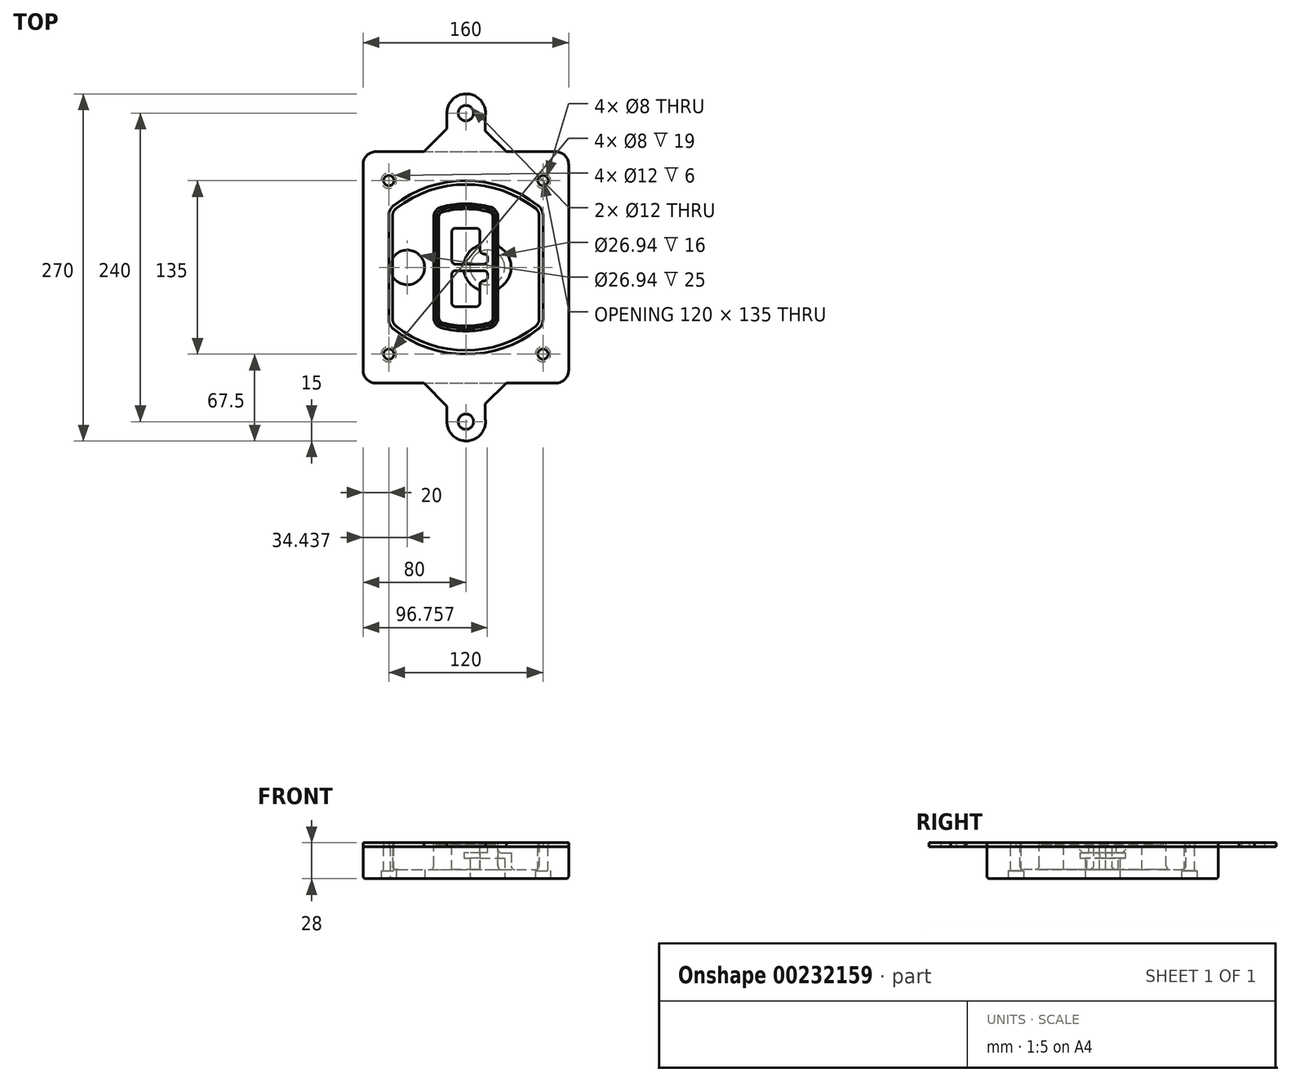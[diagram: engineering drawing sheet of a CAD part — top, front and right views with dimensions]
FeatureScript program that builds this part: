
annotation { "Feature Type Name" : "Feature", "Feature Type Description" : "" }
export const myFeature = defineFeature(function(context is Context, id is Id, definition is map)
    precondition{}
    {
        {
            var Q0;
            Q0=qCreatedBy(makeId("Top.planeOp"),FACE);
            var sketch = newSketch(context, id + "F0", { "sketchPlane" : qUnion([Q0])});
            skPoint(sketch, "E0.rect.middle", {"position": v(0, 0) * mm});
            skLineSegment(sketch, "E1.bottom", {"start": v(-70, -90) * mm, "end": v(70, -90) * mm});
            skLineSegment(sketch, "E1.top", {"start": v(-70, 90) * mm, "end": v(70, 90) * mm});
            skLineSegment(sketch, "E1.left", {"start": v(-80, -80) * mm, "end": v(-80, 80) * mm});
            skLineSegment(sketch, "E1.right", {"start": v(80, -80) * mm, "end": v(80, 80) * mm});
            skLineSegment(sketch, "E2", {"start": v(-80, 90) * mm, "end": v(80, -90) * mm, "construction": true});
            skLineSegment(sketch, "E3", {"start": v(80, 90) * mm, "end": v(-80, -90) * mm, "construction": true});
            skCircle(sketch, "E4", {"center": v(-60, 67.5) * mm, "radius": 4 * mm});
            skCircle(sketch, "E5", {"center": v(60, 67.5) * mm, "radius": 4 * mm});
            skCircle(sketch, "E6", {"center": v(60, -67.5) * mm, "radius": 4 * mm});
            skCircle(sketch, "E7", {"center": v(-60, -67.5) * mm, "radius": 4 * mm});
            skLineSegment(sketch, "E8", {"start": v(-60, 67.5) * mm, "end": v(60, 67.5) * mm, "construction": true});
            skLineSegment(sketch, "E9", {"start": v(60, 67.5) * mm, "end": v(60, -67.5) * mm, "construction": true});
            skLineSegment(sketch, "E10", {"start": v(60, -67.5) * mm, "end": v(-60, -67.5) * mm, "construction": true});
            skLineSegment(sketch, "E11", {"start": v(-60, -67.5) * mm, "end": v(-60, 67.5) * mm, "construction": true});
            skLineSegment(sketch, "E12", {"start": v(-60, 40.3) * mm, "end": v(-60, -40.3) * mm});
            skLineSegment(sketch, "E13", {"start": v(60, 40.3) * mm, "end": v(60, -40.3) * mm});
            skArc(sketch, "E14", {"start": v(56.15, 48.18) * mm, "mid": v(0, 67.5) * mm, "end": v(-56.15, 48.18) * mm});
            skArc(sketch, "E15", {"start": v(-56.15, -48.18) * mm, "mid": v(0, -67.5) * mm, "end": v(56.15, -48.18) * mm});
            skLineSegment(sketch, "E16", {"start": v(-60, 0) * mm, "end": v(60, 0) * mm, "construction": true});
            skPoint(sketch, "E17.visualSharp", {"position": v(-60, -45) * mm});
            skArc(sketch, "E17.filletArc", {"start": v(-60, -40.3) * mm, "mid": v(-58.99, -44.68) * mm, "end": v(-56.15, -48.18) * mm});
            skPoint(sketch, "E18.visualSharp", {"position": v(-60, 45) * mm});
            skArc(sketch, "E18.filletArc", {"start": v(-56.15, 48.18) * mm, "mid": v(-58.99, 44.68) * mm, "end": v(-60, 40.3) * mm});
            skPoint(sketch, "E19.visualSharp", {"position": v(60, 45) * mm});
            skArc(sketch, "E19.filletArc", {"start": v(60, 40.3) * mm, "mid": v(58.99, 44.68) * mm, "end": v(56.15, 48.18) * mm});
            skPoint(sketch, "E20.visualSharp", {"position": v(60, -45) * mm});
            skArc(sketch, "E20.filletArc", {"start": v(56.15, -48.18) * mm, "mid": v(58.99, -44.68) * mm, "end": v(60, -40.3) * mm});
            skPoint(sketch, "E21.visualSharp", {"position": v(-80, 90) * mm});
            skArc(sketch, "E21.filletArc", {"start": v(-70, 90) * mm, "mid": v(-77.07, 87.07) * mm, "end": v(-80, 80) * mm});
            skPoint(sketch, "E22.visualSharp", {"position": v(80, 90) * mm});
            skArc(sketch, "E22.filletArc", {"start": v(80, 80) * mm, "mid": v(77.07, 87.07) * mm, "end": v(70, 90) * mm});
            skPoint(sketch, "E23.visualSharp", {"position": v(80, -90) * mm});
            skArc(sketch, "E23.filletArc", {"start": v(70, -90) * mm, "mid": v(77.07, -87.07) * mm, "end": v(80, -80) * mm});
            skPoint(sketch, "E24.visualSharp", {"position": v(-80, -90) * mm});
            skArc(sketch, "E24.filletArc", {"start": v(-80, -80) * mm, "mid": v(-77.07, -87.07) * mm, "end": v(-70, -90) * mm});
            skArc(sketch, "E25.0", {"start": v(57, 40.3) * mm, "mid": v(56.3, 43.36) * mm, "end": v(54.3, 45.81) * mm});
            skLineSegment(sketch, "E25.1", {"start": v(57, 40.3) * mm, "end": v(57, -40.3) * mm});
            skArc(sketch, "E25.2", {"start": v(54.3, -45.81) * mm, "mid": v(56.3, -43.36) * mm, "end": v(57, -40.3) * mm});
            skArc(sketch, "E25.3", {"start": v(-54.3, -45.81) * mm, "mid": v(0, -64.5) * mm, "end": v(54.3, -45.81) * mm});
            skArc(sketch, "E25.4", {"start": v(-57, -40.3) * mm, "mid": v(-56.3, -43.36) * mm, "end": v(-54.3, -45.81) * mm});
            skArc(sketch, "E25.5", {"start": v(54.3, 45.81) * mm, "mid": v(0, 64.5) * mm, "end": v(-54.3, 45.81) * mm});
            skLineSegment(sketch, "E25.6", {"start": v(-57, 40.3) * mm, "end": v(-57, -40.3) * mm});
            skArc(sketch, "E25.7", {"start": v(-54.3, 45.81) * mm, "mid": v(-56.3, 43.36) * mm, "end": v(-57, 40.3) * mm});
            skArc(sketch, "E26.0", {"start": v(-58.62, 51.33) * mm, "mid": v(-62.58, 46.43) * mm, "end": v(-64, 40.3) * mm});
            skArc(sketch, "E26.1", {"start": v(58.62, 51.33) * mm, "mid": v(0, 71.5) * mm, "end": v(-58.62, 51.33) * mm});
            skArc(sketch, "E26.2", {"start": v(64, 40.3) * mm, "mid": v(62.58, 46.43) * mm, "end": v(58.62, 51.33) * mm});
            skLineSegment(sketch, "E26.3", {"start": v(64, 40.3) * mm, "end": v(64, -40.3) * mm});
            skArc(sketch, "E26.4", {"start": v(58.62, -51.33) * mm, "mid": v(62.58, -46.43) * mm, "end": v(64, -40.3) * mm});
            skLineSegment(sketch, "E26.5", {"start": v(-64, 40.3) * mm, "end": v(-64, -40.3) * mm});
            skArc(sketch, "E26.6", {"start": v(-58.62, -51.33) * mm, "mid": v(0, -71.5) * mm, "end": v(58.62, -51.33) * mm});
            skArc(sketch, "E26.7", {"start": v(-64, -40.3) * mm, "mid": v(-62.58, -46.43) * mm, "end": v(-58.62, -51.33) * mm});
            skSolve(sketch);
        }
        {
            var Q0;
            Q0=makeQuery(id+"F0.imprint","IMPRINT",FACE,{"disambiguationData":[TD([[makeQuery(id+"F0.imprint","IMPRINT",EDGE,{"derivedFrom":sQuery(id+"F0.wireOp",EDGE,"E1.bottom")}),1.0]])]});
            var Q1;
            Q1=makeQuery(id+"F0.imprint","IMPRINT",FACE,{"disambiguationData":[TD([[makeQuery(id+"F0.imprint","IMPRINT",EDGE,{"derivedFrom":sQuery(id+"F0.wireOp",EDGE,"E12")}),1.0]])]});
            var Q2;
            Q2=makeQuery(id+"F0.imprint","IMPRINT",FACE,{"disambiguationData":[TD([[makeQuery(id+"F0.imprint","IMPRINT",EDGE,{"derivedFrom":sQuery(id+"F0.wireOp",EDGE,"E25.0")}),1.0]])]});
            var Q3;
            Q3=makeQuery(id+"F0.imprint","IMPRINT",FACE,{"disambiguationData":[TD([[makeQuery(id+"F0.imprint","IMPRINT",EDGE,{"derivedFrom":sQuery(id+"F0.wireOp",EDGE,"E12")}),-1.0]])]});
            extrude(context, id + "F1", {"entities" : qUnion([Q0, Q1, Q2, Q3]), "oppositeDirection" : true, "depth" : 25 * mm});
        }
        {
            var Q0;
            Q0=makeQuery(id+"F0.imprint","IMPRINT",FACE,{"disambiguationData":[TD([[makeQuery(id+"F0.imprint","IMPRINT",EDGE,{"derivedFrom":sQuery(id+"F0.wireOp",EDGE,"E12")}),1.0]])]});
            extrude(context, id + "F2", {"entities" : qUnion([Q0]), "operationType" : NewBodyOperationType.ADD, "depth" : 3 * mm});
        }
        {
            var Q0;
            Q0=makeQuery(id+"F0.imprint","IMPRINT",FACE,{"disambiguationData":[TD([[makeQuery(id+"F0.imprint","IMPRINT",EDGE,{"derivedFrom":sQuery(id+"F0.wireOp",EDGE,"E25.0")}),1.0]])]});
            extrude(context, id + "F3", {"entities" : qUnion([Q0]), "operationType" : NewBodyOperationType.REMOVE, "oppositeDirection" : true, "depth" : 18 * mm});
        }
        {
            var Q0;
            Q0=makeQuery(id+"F2.opExtrude","CAP_FACE",FACE,{"disambiguationData":[OSD([sQuery(id+"F0.wireOp",EDGE,"E12"),sQuery(id+"F0.wireOp",EDGE,"E13"),sQuery(id+"F0.wireOp",EDGE,"E14"),sQuery(id+"F0.wireOp",EDGE,"E15"),sQuery(id+"F0.wireOp",EDGE,"E17.filletArc"),sQuery(id+"F0.wireOp",EDGE,"E18.filletArc"),sQuery(id+"F0.wireOp",EDGE,"E19.filletArc"),sQuery(id+"F0.wireOp",EDGE,"E20.filletArc"),sQuery(id+"F0.wireOp",EDGE,"E25.0"),sQuery(id+"F0.wireOp",EDGE,"E25.1"),sQuery(id+"F0.wireOp",EDGE,"E25.2"),sQuery(id+"F0.wireOp",EDGE,"E25.3"),sQuery(id+"F0.wireOp",EDGE,"E25.4"),sQuery(id+"F0.wireOp",EDGE,"E25.5"),sQuery(id+"F0.wireOp",EDGE,"E25.6"),sQuery(id+"F0.wireOp",EDGE,"E25.7")])],"isStart":false});
            var sketch = newSketch(context, id + "F4", { "sketchPlane" : qUnion([Q0])});
            skArc(sketch, "E27.0", {"start": v(-19.08, -46.97) * mm, "mid": v(0, -49.5) * mm, "end": v(19.08, -46.97) * mm});
            skArc(sketch, "E28.0", {"start": v(19.08, 46.97) * mm, "mid": v(0, 49.5) * mm, "end": v(-19.08, 46.97) * mm});
            skLineSegment(sketch, "E29", {"start": v(-25, 39.25) * mm, "end": v(-25, -39.25) * mm});
            skLineSegment(sketch, "E30", {"start": v(25, 39.25) * mm, "end": v(25, -39.25) * mm});
            skLineSegment(sketch, "E31", {"start": v(-25, 45.1) * mm, "end": v(25, 45.1) * mm, "construction": true});
            skLineSegment(sketch, "E32", {"start": v(-25, -45.1) * mm, "end": v(25, -45.1) * mm, "construction": true});
            skPoint(sketch, "E33.visualSharp", {"position": v(-25, 45.1) * mm});
            skArc(sketch, "E33.filletArc", {"start": v(-19.08, 46.97) * mm, "mid": v(-23.35, 44.11) * mm, "end": v(-25, 39.25) * mm});
            skPoint(sketch, "E34.visualSharp", {"position": v(25, 45.1) * mm});
            skArc(sketch, "E34.filletArc", {"start": v(25, 39.25) * mm, "mid": v(23.35, 44.11) * mm, "end": v(19.08, 46.97) * mm});
            skPoint(sketch, "E35.visualSharp", {"position": v(25, -45.1) * mm});
            skArc(sketch, "E35.filletArc", {"start": v(19.08, -46.97) * mm, "mid": v(23.35, -44.11) * mm, "end": v(25, -39.25) * mm});
            skPoint(sketch, "E36.visualSharp", {"position": v(-25, -45.1) * mm});
            skArc(sketch, "E36.filletArc", {"start": v(-25, -39.25) * mm, "mid": v(-23.35, -44.11) * mm, "end": v(-19.08, -46.97) * mm});
            skArc(sketch, "E37.0", {"start": v(54.3, 45.81) * mm, "mid": v(0, 64.5) * mm, "end": v(-54.3, 45.81) * mm});
            skArc(sketch, "E37.1", {"start": v(-54.3, 45.81) * mm, "mid": v(-56.3, 43.36) * mm, "end": v(-57, 40.3) * mm});
            skLineSegment(sketch, "E37.2", {"start": v(-57, 40.3) * mm, "end": v(-57, -40.3) * mm});
            skArc(sketch, "E37.3", {"start": v(-57, -40.3) * mm, "mid": v(-56.3, -43.36) * mm, "end": v(-54.3, -45.81) * mm});
            skArc(sketch, "E37.4", {"start": v(-54.3, -45.81) * mm, "mid": v(0, -64.5) * mm, "end": v(54.3, -45.81) * mm});
            skArc(sketch, "E37.5", {"start": v(54.3, -45.81) * mm, "mid": v(56.3, -43.36) * mm, "end": v(57, -40.3) * mm});
            skLineSegment(sketch, "E37.6", {"start": v(57, 40.3) * mm, "end": v(57, -40.3) * mm});
            skArc(sketch, "E37.7", {"start": v(57, 40.3) * mm, "mid": v(56.3, 43.36) * mm, "end": v(54.3, 45.81) * mm});
            skLineSegment(sketch, "E38.0", {"start": v(23, 39.25) * mm, "end": v(23, -39.25) * mm});
            skArc(sketch, "E38.1", {"start": v(18.56, -45.04) * mm, "mid": v(21.76, -42.9) * mm, "end": v(23, -39.25) * mm});
            skArc(sketch, "E38.2", {"start": v(-18.56, -45.04) * mm, "mid": v(0, -47.5) * mm, "end": v(18.56, -45.04) * mm});
            skArc(sketch, "E38.3", {"start": v(-23, -39.25) * mm, "mid": v(-21.76, -42.9) * mm, "end": v(-18.56, -45.04) * mm});
            skLineSegment(sketch, "E38.4", {"start": v(-23, 39.25) * mm, "end": v(-23, -39.25) * mm});
            skArc(sketch, "E38.5", {"start": v(23, 39.25) * mm, "mid": v(21.76, 42.9) * mm, "end": v(18.56, 45.04) * mm});
            skArc(sketch, "E38.6", {"start": v(-18.56, 45.04) * mm, "mid": v(-21.76, 42.9) * mm, "end": v(-23, 39.25) * mm});
            skArc(sketch, "E38.7", {"start": v(18.56, 45.04) * mm, "mid": v(0, 47.5) * mm, "end": v(-18.56, 45.04) * mm});
            skArc(sketch, "E39.0", {"start": v(21, 39.25) * mm, "mid": v(20.18, 41.68) * mm, "end": v(18.04, 43.1) * mm});
            skLineSegment(sketch, "E39.1", {"start": v(21, 39.25) * mm, "end": v(21, -39.25) * mm});
            skArc(sketch, "E39.2", {"start": v(18.04, -43.1) * mm, "mid": v(20.18, -41.68) * mm, "end": v(21, -39.25) * mm});
            skArc(sketch, "E39.3", {"start": v(-18.04, -43.1) * mm, "mid": v(0, -45.5) * mm, "end": v(18.04, -43.1) * mm});
            skArc(sketch, "E39.4", {"start": v(-21, -39.25) * mm, "mid": v(-20.18, -41.68) * mm, "end": v(-18.04, -43.1) * mm});
            skArc(sketch, "E39.5", {"start": v(18.04, 43.1) * mm, "mid": v(0, 45.5) * mm, "end": v(-18.04, 43.1) * mm});
            skLineSegment(sketch, "E39.6", {"start": v(-21, 39.25) * mm, "end": v(-21, -39.25) * mm});
            skArc(sketch, "E39.7", {"start": v(-18.04, 43.1) * mm, "mid": v(-20.18, 41.68) * mm, "end": v(-21, 39.25) * mm});
            skLineSegment(sketch, "E40", {"start": v(-25, 0) * mm, "end": v(25, 0) * mm, "construction": true});
            skLineSegment(sketch, "E41", {"start": v(-11, 5.5) * mm, "end": v(-11, 27.5) * mm});
            skLineSegment(sketch, "E42", {"start": v(-8, 30.5) * mm, "end": v(8, 30.5) * mm});
            skLineSegment(sketch, "E43", {"start": v(11, 27.5) * mm, "end": v(11, 13.5) * mm});
            skLineSegment(sketch, "E44", {"start": v(14, 10.5) * mm, "end": v(14, 10.5) * mm});
            skLineSegment(sketch, "E45", {"start": v(17, 7.5) * mm, "end": v(17, 5.5) * mm});
            skLineSegment(sketch, "E46", {"start": v(14, 2.5) * mm, "end": v(-8, 2.5) * mm});
            skPoint(sketch, "E47.visualSharp", {"position": v(-11, 30.5) * mm});
            skArc(sketch, "E47.filletArc", {"start": v(-8, 30.5) * mm, "mid": v(-10.12, 29.62) * mm, "end": v(-11, 27.5) * mm});
            skPoint(sketch, "E48.visualSharp", {"position": v(11, 30.5) * mm});
            skArc(sketch, "E48.filletArc", {"start": v(11, 27.5) * mm, "mid": v(10.12, 29.62) * mm, "end": v(8, 30.5) * mm});
            skPoint(sketch, "E49.visualSharp", {"position": v(11, 10.5) * mm});
            skArc(sketch, "E49.filletArc", {"start": v(11, 13.5) * mm, "mid": v(11.88, 11.38) * mm, "end": v(14, 10.5) * mm});
            skPoint(sketch, "E50.visualSharp", {"position": v(17, 10.5) * mm});
            skArc(sketch, "E50.filletArc", {"start": v(17, 7.5) * mm, "mid": v(16.12, 9.62) * mm, "end": v(14, 10.5) * mm});
            skPoint(sketch, "E51.visualSharp", {"position": v(17, 2.5) * mm});
            skArc(sketch, "E51.filletArc", {"start": v(14, 2.5) * mm, "mid": v(16.12, 3.38) * mm, "end": v(17, 5.5) * mm});
            skPoint(sketch, "E52.visualSharp", {"position": v(-11, 2.5) * mm});
            skArc(sketch, "E52.filletArc", {"start": v(-11, 5.5) * mm, "mid": v(-10.12, 3.38) * mm, "end": v(-8, 2.5) * mm});
            skLineSegment(sketch, "E53.0.MirrorCS", {"start": v(14, -2.5) * mm, "end": v(-8, -2.5) * mm});
            skArc(sketch, "E54.0.MirrorCS", {"start": v(-11, -5.5) * mm, "mid": v(-10.12, -3.38) * mm, "end": v(-8, -2.5) * mm});
            skLineSegment(sketch, "E55.0.MirrorCS", {"start": v(-11, -5.5) * mm, "end": v(-11, -27.5) * mm});
            skArc(sketch, "E56.0.MirrorCS", {"start": v(-8, -30.5) * mm, "mid": v(-10.12, -29.62) * mm, "end": v(-11, -27.5) * mm});
            skLineSegment(sketch, "E57.0.MirrorCS", {"start": v(-8, -30.5) * mm, "end": v(8, -30.5) * mm});
            skArc(sketch, "E58.0.MirrorCS", {"start": v(11, -27.5) * mm, "mid": v(10.12, -29.62) * mm, "end": v(8, -30.5) * mm});
            skLineSegment(sketch, "E59.0.MirrorCS", {"start": v(11, -27.5) * mm, "end": v(11, -13.5) * mm});
            skArc(sketch, "E60.0.MirrorCS", {"start": v(11, -13.5) * mm, "mid": v(11.88, -11.38) * mm, "end": v(14, -10.5) * mm});
            skArc(sketch, "E61.0.MirrorCS", {"start": v(17, -7.5) * mm, "mid": v(16.12, -9.62) * mm, "end": v(14, -10.5) * mm});
            skLineSegment(sketch, "E62.0.MirrorCS", {"start": v(17, -7.5) * mm, "end": v(17, -5.5) * mm});
            skArc(sketch, "E63.0.MirrorCS", {"start": v(14, -2.5) * mm, "mid": v(16.12, -3.38) * mm, "end": v(17, -5.5) * mm});
            skSolve(sketch);
        }
        {
            var Q0;
            Q0=makeQuery(id+"F4.imprint","IMPRINT",FACE,{"disambiguationData":[TD([[makeQuery(id+"F4.imprint","IMPRINT",EDGE,{"derivedFrom":sQuery(id+"F4.wireOp",EDGE,"E27.0")}),1.0]])]});
            var Q1;
            Q1=makeQuery(id+"F4.imprint","IMPRINT",FACE,{"disambiguationData":[TD([[makeQuery(id+"F4.imprint","IMPRINT",EDGE,{"derivedFrom":sQuery(id+"F4.wireOp",EDGE,"E38.0")}),-1.0]])]});
            var Q2;
            Q2=makeQuery(id+"F4.imprint","IMPRINT",FACE,{"disambiguationData":[TD([[makeQuery(id+"F4.imprint","IMPRINT",EDGE,{"derivedFrom":sQuery(id+"F4.wireOp",EDGE,"E39.0")}),1.0]])]});
            extrude(context, id + "F5", {"entities" : qUnion([Q0, Q1, Q2]), "operationType" : NewBodyOperationType.ADD, "endBound" : BoundingType.UP_TO_NEXT, "oppositeDirection" : true, "depth" : 25 * mm});
        }
        {
            var Q0;
            Q0=makeQuery(id+"F4.imprint","IMPRINT",FACE,{"disambiguationData":[TD([[makeQuery(id+"F4.imprint","IMPRINT",EDGE,{"derivedFrom":sQuery(id+"F4.wireOp",EDGE,"E38.0")}),-1.0]])]});
            extrude(context, id + "F6", {"entities" : qUnion([Q0]), "operationType" : NewBodyOperationType.REMOVE, "oppositeDirection" : true, "depth" : 2 * mm});
        }
        {
            var Q0;
            Q0=makeQuery(id+"F1.opExtrude","CAP_FACE",FACE,{"disambiguationData":[OSD([sQuery(id+"F0.wireOp",EDGE,"E1.bottom"),sQuery(id+"F0.wireOp",EDGE,"E1.top"),sQuery(id+"F0.wireOp",EDGE,"E1.left"),sQuery(id+"F0.wireOp",EDGE,"E1.right"),sQuery(id+"F0.wireOp",EDGE,"E4"),sQuery(id+"F0.wireOp",EDGE,"E5"),sQuery(id+"F0.wireOp",EDGE,"E6"),sQuery(id+"F0.wireOp",EDGE,"E7"),sQuery(id+"F0.wireOp",EDGE,"E21.filletArc"),sQuery(id+"F0.wireOp",EDGE,"E22.filletArc"),sQuery(id+"F0.wireOp",EDGE,"E23.filletArc"),sQuery(id+"F0.wireOp",EDGE,"E24.filletArc")])],"isStart":false});
            var sketch = newSketch(context, id + "F7", { "sketchPlane" : qUnion([Q0])});
            skCircle(sketch, "E64", {"center": v(16.76, 0) * mm, "radius": 13.47 * mm});
            skCircle(sketch, "E65", {"center": v(-45.56, 0) * mm, "radius": 13.47 * mm});
            skLineSegment(sketch, "E66", {"start": v(80, 0) * mm, "end": v(-80, 0) * mm});
            skCircle(sketch, "E67", {"center": v(16.76, 0) * mm, "radius": 18.47 * mm});
            skCircle(sketch, "E68", {"center": v(60, -67.5) * mm, "radius": 6 * mm});
            skCircle(sketch, "E69", {"center": v(-60, -67.5) * mm, "radius": 6 * mm});
            skCircle(sketch, "E70", {"center": v(-60, 67.5) * mm, "radius": 6 * mm});
            skCircle(sketch, "E71", {"center": v(60, 67.5) * mm, "radius": 6 * mm});
            skSolve(sketch);
        }
        {
            var Q0;
            {var subQ1=sQuery(id+"F7.wireOp",EDGE,"E66");var subQ4=sQuery(id+"F7.wireOp",EDGE,"E64");var subQ6=makeQuery(id+"F7.imprint","INTERSECT",VERTEX,{"disambiguationData":[OD(0.0)],"derivedFrom":[subQ4,subQ1]});Q0=makeQuery(id+"F7.imprint","IMPRINT",FACE,{"disambiguationData":[TD([[makeQuery(id+"F7.imprint","IMPRINT",EDGE,{"disambiguationData":[TD([[subQ6,-1.0]])],"derivedFrom":subQ4}),-1.0]])]});}
            var Q1;
            {var subQ0=sQuery(id+"F7.wireOp",EDGE,"E66");var subQ1=sQuery(id+"F7.wireOp",EDGE,"E64");var subQ3=makeQuery(id+"F7.imprint","INTERSECT",VERTEX,{"disambiguationData":[OD(0.0)],"derivedFrom":[subQ1,subQ0]});Q1=makeQuery(id+"F7.imprint","IMPRINT",FACE,{"disambiguationData":[TD([[makeQuery(id+"F7.imprint","IMPRINT",EDGE,{"disambiguationData":[TD([[subQ3,-1.0]])],"derivedFrom":subQ1}),1.0]])]});}
            var Q2;
            {var subQ0=sQuery(id+"F7.wireOp",EDGE,"E66");var subQ1=sQuery(id+"F7.wireOp",EDGE,"E64");var subQ3=makeQuery(id+"F7.imprint","INTERSECT",VERTEX,{"disambiguationData":[OD(0.0)],"derivedFrom":[subQ1,subQ0]});Q2=makeQuery(id+"F7.imprint","IMPRINT",FACE,{"disambiguationData":[TD([[makeQuery(id+"F7.imprint","IMPRINT",EDGE,{"disambiguationData":[TD([[subQ3,1.0]])],"derivedFrom":subQ1}),1.0]])]});}
            var Q3;
            {var subQ1=sQuery(id+"F7.wireOp",EDGE,"E66");var subQ4=sQuery(id+"F7.wireOp",EDGE,"E64");var subQ6=makeQuery(id+"F7.imprint","INTERSECT",VERTEX,{"disambiguationData":[OD(0.0)],"derivedFrom":[subQ4,subQ1]});Q3=makeQuery(id+"F7.imprint","IMPRINT",FACE,{"disambiguationData":[TD([[makeQuery(id+"F7.imprint","IMPRINT",EDGE,{"disambiguationData":[TD([[subQ6,1.0]])],"derivedFrom":subQ4}),-1.0]])]});}
            extrude(context, id + "F8", {"entities" : qUnion([Q0, Q1, Q2, Q3]), "operationType" : NewBodyOperationType.ADD, "oppositeDirection" : true, "depth" : 20 * mm});
        }
        {
            var Q0;
            {var subQ0=sQuery(id+"F7.wireOp",EDGE,"E66");var subQ1=sQuery(id+"F7.wireOp",EDGE,"E64");var subQ3=makeQuery(id+"F7.imprint","INTERSECT",VERTEX,{"disambiguationData":[OD(0.0)],"derivedFrom":[subQ1,subQ0]});Q0=makeQuery(id+"F7.imprint","IMPRINT",FACE,{"disambiguationData":[TD([[makeQuery(id+"F7.imprint","IMPRINT",EDGE,{"disambiguationData":[TD([[subQ3,-1.0]])],"derivedFrom":subQ1}),1.0]])]});}
            var Q1;
            {var subQ0=sQuery(id+"F7.wireOp",EDGE,"E66");var subQ1=sQuery(id+"F7.wireOp",EDGE,"E64");var subQ3=makeQuery(id+"F7.imprint","INTERSECT",VERTEX,{"disambiguationData":[OD(0.0)],"derivedFrom":[subQ1,subQ0]});Q1=makeQuery(id+"F7.imprint","IMPRINT",FACE,{"disambiguationData":[TD([[makeQuery(id+"F7.imprint","IMPRINT",EDGE,{"disambiguationData":[TD([[subQ3,1.0]])],"derivedFrom":subQ1}),1.0]])]});}
            extrude(context, id + "F9", {"entities" : qUnion([Q0, Q1]), "operationType" : NewBodyOperationType.REMOVE, "oppositeDirection" : true, "depth" : 16 * mm});
        }
        {
            var Q0;
            {var subQ0=sQuery(id+"F7.wireOp",EDGE,"E66");var subQ1=sQuery(id+"F7.wireOp",EDGE,"E65");var subQ3=makeQuery(id+"F7.imprint","INTERSECT",VERTEX,{"disambiguationData":[OD(0.0)],"derivedFrom":[subQ1,subQ0]});Q0=makeQuery(id+"F7.imprint","IMPRINT",FACE,{"disambiguationData":[TD([[makeQuery(id+"F7.imprint","IMPRINT",EDGE,{"disambiguationData":[TD([[subQ3,-1.0]])],"derivedFrom":subQ1}),1.0]])]});}
            var Q1;
            {var subQ0=sQuery(id+"F7.wireOp",EDGE,"E66");var subQ1=sQuery(id+"F7.wireOp",EDGE,"E65");var subQ3=makeQuery(id+"F7.imprint","INTERSECT",VERTEX,{"disambiguationData":[OD(0.0)],"derivedFrom":[subQ1,subQ0]});Q1=makeQuery(id+"F7.imprint","IMPRINT",FACE,{"disambiguationData":[TD([[makeQuery(id+"F7.imprint","IMPRINT",EDGE,{"disambiguationData":[TD([[subQ3,1.0]])],"derivedFrom":subQ1}),1.0]])]});}
            extrude(context, id + "F10", {"entities" : qUnion([Q0, Q1]), "operationType" : NewBodyOperationType.REMOVE, "oppositeDirection" : true, "depth" : 25 * mm});
        }
        {
            var Q0;
            Q0=makeQuery(id+"F7.imprint","IMPRINT",FACE,{"disambiguationData":[TD([[makeQuery(id+"F7.imprint","IMPRINT",EDGE,{"derivedFrom":sQuery(id+"F7.wireOp",EDGE,"E68")}),1.0]])]});
            var Q1;
            Q1=makeQuery(id+"F7.imprint","IMPRINT",FACE,{"disambiguationData":[TD([[makeQuery(id+"F7.imprint","IMPRINT",EDGE,{"derivedFrom":makeQuery(id+"F1.opExtrude","CAP_EDGE",EDGE,{"disambiguationData":[OSD([sQuery(id+"F0.wireOp",EDGE,"E5")])],"isStart":false})}),-1.0]])]});
            var Q2;
            Q2=makeQuery(id+"F7.imprint","IMPRINT",FACE,{"disambiguationData":[TD([[makeQuery(id+"F7.imprint","IMPRINT",EDGE,{"derivedFrom":sQuery(id+"F7.wireOp",EDGE,"E69")}),1.0]])]});
            var Q3;
            Q3=makeQuery(id+"F7.imprint","IMPRINT",FACE,{"disambiguationData":[TD([[makeQuery(id+"F7.imprint","IMPRINT",EDGE,{"derivedFrom":makeQuery(id+"F1.opExtrude","CAP_EDGE",EDGE,{"disambiguationData":[OSD([sQuery(id+"F0.wireOp",EDGE,"E4")])],"isStart":false})}),-1.0]])]});
            var Q4;
            Q4=makeQuery(id+"F7.imprint","IMPRINT",FACE,{"disambiguationData":[TD([[makeQuery(id+"F7.imprint","IMPRINT",EDGE,{"derivedFrom":sQuery(id+"F7.wireOp",EDGE,"E70")}),1.0]])]});
            var Q5;
            Q5=makeQuery(id+"F7.imprint","IMPRINT",FACE,{"disambiguationData":[TD([[makeQuery(id+"F7.imprint","IMPRINT",EDGE,{"derivedFrom":makeQuery(id+"F1.opExtrude","CAP_EDGE",EDGE,{"disambiguationData":[OSD([sQuery(id+"F0.wireOp",EDGE,"E7")])],"isStart":false})}),-1.0]])]});
            var Q6;
            Q6=makeQuery(id+"F7.imprint","IMPRINT",FACE,{"disambiguationData":[TD([[makeQuery(id+"F7.imprint","IMPRINT",EDGE,{"derivedFrom":sQuery(id+"F7.wireOp",EDGE,"E71")}),1.0]])]});
            var Q7;
            Q7=makeQuery(id+"F7.imprint","IMPRINT",FACE,{"disambiguationData":[TD([[makeQuery(id+"F7.imprint","IMPRINT",EDGE,{"derivedFrom":makeQuery(id+"F1.opExtrude","CAP_EDGE",EDGE,{"disambiguationData":[OSD([sQuery(id+"F0.wireOp",EDGE,"E6")])],"isStart":false})}),-1.0]])]});
            extrude(context, id + "F11", {"entities" : qUnion([Q0, Q1, Q2, Q3, Q4, Q5, Q6, Q7]), "operationType" : NewBodyOperationType.REMOVE, "oppositeDirection" : true, "depth" : 6 * mm});
        }
        {
            var Q0;
            Q0=makeQuery(id+"F9.boolean.opBoolean","COPY",FACE,{"derivedFrom":makeQuery(id+"F9.opExtrude","CAP_FACE",FACE,{"disambiguationData":[OSD([sQuery(id+"F7.wireOp",EDGE,"E64")])],"isStart":false})});
            var sketch = newSketch(context, id + "F12", { "sketchPlane" : qUnion([Q0])});
            skArc(sketch, "E72.0", {"start": v(11, 17.55) * mm, "mid": v(2.57, 11.82) * mm, "end": v(-1.54, 2.5) * mm});
            skArc(sketch, "E72.1", {"start": v(-1.54, -2.5) * mm, "mid": v(2.57, -11.82) * mm, "end": v(11, -17.55) * mm});
            skLineSegment(sketch, "E73", {"start": v(-1.54, -2.5) * mm, "end": v(14, -2.5) * mm});
            skLineSegment(sketch, "E74.0", {"start": v(14, 2.5) * mm, "end": v(-1.54, 2.5) * mm});
            skArc(sketch, "E74.1", {"start": v(14, 2.5) * mm, "mid": v(16.12, 3.38) * mm, "end": v(17, 5.5) * mm});
            skLineSegment(sketch, "E74.2", {"start": v(17, 7.5) * mm, "end": v(17, 5.5) * mm});
            skArc(sketch, "E74.3", {"start": v(17, 7.5) * mm, "mid": v(16.12, 9.62) * mm, "end": v(14, 10.5) * mm});
            skArc(sketch, "E74.4", {"start": v(11, 13.5) * mm, "mid": v(11.88, 11.38) * mm, "end": v(14, 10.5) * mm});
            skLineSegment(sketch, "E74.5", {"start": v(11, 17.55) * mm, "end": v(11, 13.5) * mm});
            skLineSegment(sketch, "E74.7", {"start": v(14, -2.5) * mm, "end": v(-1.54, -2.5) * mm});
            skArc(sketch, "E74.8", {"start": v(14, -2.5) * mm, "mid": v(16.12, -3.38) * mm, "end": v(17, -5.5) * mm});
            skLineSegment(sketch, "E74.9", {"start": v(17, -7.5) * mm, "end": v(17, -5.5) * mm});
            skArc(sketch, "E74.10", {"start": v(17, -7.5) * mm, "mid": v(16.12, -9.62) * mm, "end": v(14, -10.5) * mm});
            skArc(sketch, "E74.11", {"start": v(11, -13.5) * mm, "mid": v(11.88, -11.38) * mm, "end": v(14, -10.5) * mm});
            skLineSegment(sketch, "E74.12", {"start": v(11, -17.55) * mm, "end": v(11, -13.5) * mm});
            skPoint(sketch, "E75.orphan", {"position": v(11, -27.5) * mm});
            skPoint(sketch, "E76.orphan", {"position": v(-8, -2.5) * mm});
            skPoint(sketch, "E77.orphan", {"position": v(-8, 2.5) * mm});
            skPoint(sketch, "E78.orphan", {"position": v(11, 27.5) * mm});
            skSolve(sketch);
        }
        {
            var Q0;
            {var subQ7=sQuery(id+"F12.wireOp",EDGE,"E72.0");var subQ14=sQuery(id+"F12.wireOp",EDGE,"E72.1");var subQ16=sQuery(id+"F12.wireOp",EDGE,"E74.1");var subQ18=sQuery(id+"F12.wireOp",EDGE,"E74.8");Q0=qUnion([makeQuery(id+"F12.imprint","IMPRINT",FACE,{"disambiguationData":[TD([[makeQuery(id+"F12.imprint","IMPRINT",EDGE,{"derivedFrom":subQ7}),1.0]])]}),makeQuery(id+"F12.imprint","IMPRINT",FACE,{"disambiguationData":[TD([[makeQuery(id+"F12.imprint","IMPRINT",EDGE,{"derivedFrom":subQ14}),1.0]])]}),makeQuery(id+"F12.imprint","IMPRINT",FACE,{"disambiguationData":[TD([[makeQuery(id+"F12.imprint","IMPRINT",EDGE,{"derivedFrom":subQ16}),1.0]])]}),makeQuery(id+"F12.imprint","IMPRINT",FACE,{"disambiguationData":[TD([[makeQuery(id+"F12.imprint","IMPRINT",EDGE,{"derivedFrom":subQ18}),-1.0]])]})]);}
            var Q1;
            Q1=makeQuery(id+"F5.boolean.opBoolean","SPLIT",FACE,{"disambiguationData":[TD([makeQuery(id+"F5.opExtrude","SWEPT_FACE",FACE,{"disambiguationData":[OSD([sQuery(id+"F4.wireOp",EDGE,"E41")])]})])],"derivedFrom":makeQuery(id+"F3.boolean.opBoolean","COPY",FACE,{"derivedFrom":makeQuery(id+"F3.opExtrude","CAP_FACE",FACE,{"disambiguationData":[OSD([sQuery(id+"F0.wireOp",EDGE,"E25.0"),sQuery(id+"F0.wireOp",EDGE,"E25.1"),sQuery(id+"F0.wireOp",EDGE,"E25.2"),sQuery(id+"F0.wireOp",EDGE,"E25.3"),sQuery(id+"F0.wireOp",EDGE,"E25.4"),sQuery(id+"F0.wireOp",EDGE,"E25.5"),sQuery(id+"F0.wireOp",EDGE,"E25.6"),sQuery(id+"F0.wireOp",EDGE,"E25.7")])],"isStart":false})})});
            extrude(context, id + "F13", {"entities" : qUnion([Q0]), "operationType" : NewBodyOperationType.REMOVE, "endBound" : BoundingType.UP_TO_SURFACE, "endBoundEntityFace" : qUnion([Q1]), "depth" : 25 * mm});
        }
        {
            var Q0;
            Q0=makeQuery(id+"F3.boolean.opBoolean","COPY",EDGE,{"derivedFrom":makeQuery(id+"F3.opExtrude","CAP_EDGE",EDGE,{"disambiguationData":[OSD([sQuery(id+"F0.wireOp",EDGE,"E25.6")])],"isStart":false})});
            var Q1;
            Q1=makeQuery(id+"F8.boolean.opBoolean","INTERSECT",EDGE,{"derivedFrom":[makeQuery(id+"F5.opExtrude","SWEPT_FACE",FACE,{"disambiguationData":[OSD([sQuery(id+"F4.wireOp",EDGE,"E30")])]}),makeQuery(id+"F8.opExtrude","CAP_FACE",FACE,{"disambiguationData":[OSD([sQuery(id+"F7.wireOp",EDGE,"E67")])],"isStart":false})]});
            var Q2;
            Q2=makeQuery(id+"F8.boolean.opBoolean","INTERSECT",EDGE,{"disambiguationData":[OD(1.0)],"derivedFrom":[makeQuery(id+"F5.opExtrude","SWEPT_FACE",FACE,{"disambiguationData":[OSD([sQuery(id+"F4.wireOp",EDGE,"E30")])]}),makeQuery(id+"F8.opExtrude","SWEPT_FACE",FACE,{"disambiguationData":[OSD([sQuery(id+"F7.wireOp",EDGE,"E67")])]})]});
            var Q3;
            {var subQ0=sQuery(id+"F4.wireOp",EDGE,"E30");Q3=makeQuery(id+"F8.boolean.opBoolean","SPLIT",EDGE,{"disambiguationData":[TD([makeQuery(id+"F5.opExtrude","SWEPT_FACE",FACE,{"disambiguationData":[OSD([sQuery(id+"F4.wireOp",EDGE,"E35.filletArc")])]})])],"derivedFrom":makeQuery(id+"F5.opExtrude","CAP_EDGE",EDGE,{"disambiguationData":[OSD([subQ0])],"isStart":false})});}
            var Q4;
            {var subQ0=sQuery(id+"F0.wireOp",EDGE,"E25.7");var subQ1=sQuery(id+"F0.wireOp",EDGE,"E25.1");var subQ2=sQuery(id+"F0.wireOp",EDGE,"E25.6");var subQ3=sQuery(id+"F0.wireOp",EDGE,"E25.5");var subQ4=sQuery(id+"F0.wireOp",EDGE,"E25.4");var subQ5=sQuery(id+"F0.wireOp",EDGE,"E25.0");var subQ6=sQuery(id+"F0.wireOp",EDGE,"E25.2");var subQ7=sQuery(id+"F0.wireOp",EDGE,"E25.3");Q4=makeQuery(id+"F8.boolean.opBoolean","INTERSECT",EDGE,{"derivedFrom":[makeQuery(id+"F5.boolean.opBoolean","SPLIT",FACE,{"disambiguationData":[TD([makeQuery(id+"F2.opExtrude","SWEPT_FACE",FACE,{"disambiguationData":[OSD([subQ5])]})])],"derivedFrom":makeQuery(id+"F3.boolean.opBoolean","COPY",FACE,{"derivedFrom":makeQuery(id+"F3.opExtrude","CAP_FACE",FACE,{"disambiguationData":[OSD([subQ5,subQ1,subQ6,subQ7,subQ4,subQ3,subQ2,subQ0])],"isStart":false})})}),makeQuery(id+"F8.opExtrude","SWEPT_FACE",FACE,{"disambiguationData":[OSD([sQuery(id+"F7.wireOp",EDGE,"E67")])]})]});}
            var Q5;
            Q5=makeQuery(id+"F8.boolean.opBoolean","INTERSECT",EDGE,{"disambiguationData":[OD(0.0)],"derivedFrom":[makeQuery(id+"F5.opExtrude","SWEPT_FACE",FACE,{"disambiguationData":[OSD([sQuery(id+"F4.wireOp",EDGE,"E30")])]}),makeQuery(id+"F8.opExtrude","SWEPT_FACE",FACE,{"disambiguationData":[OSD([sQuery(id+"F7.wireOp",EDGE,"E67")])]})]});
            fillet(context, id + "F14", {"entities" : qUnion([Q0, Q1, Q2, Q3, Q4, Q5]), "radius" : 3 * mm, "tangentPropagation" : true, "allowEdgeOverflow" : false});
        }
        {
            var Q0;
            Q0=makeQuery(id+"F1.opExtrude","CAP_EDGE",EDGE,{"disambiguationData":[OSD([sQuery(id+"F0.wireOp",EDGE,"E1.bottom")])],"isStart":false});
            fillet(context, id + "F15", {"entities" : qUnion([Q0]), "radius" : 2 * mm, "tangentPropagation" : true, "allowEdgeOverflow" : false});
        }
        {
            var Q0;
            Q0=qCreatedBy(makeId("Top.planeOp"),FACE);
            var sketch = newSketch(context, id + "F16", { "sketchPlane" : qUnion([Q0])});
            skLineSegment(sketch, "E79.0", {"start": v(-70, 90) * mm, "end": v(70, 90) * mm});
            skArc(sketch, "E79.1", {"start": v(-70, 90) * mm, "mid": v(-77.07, 87.07) * mm, "end": v(-80, 80) * mm});
            skLineSegment(sketch, "E79.2", {"start": v(-80, -80) * mm, "end": v(-80, 80) * mm});
            skArc(sketch, "E79.3", {"start": v(-80, -80) * mm, "mid": v(-77.07, -87.07) * mm, "end": v(-70, -90) * mm});
            skLineSegment(sketch, "E79.4", {"start": v(-70, -90) * mm, "end": v(70, -90) * mm});
            skArc(sketch, "E79.5", {"start": v(70, -90) * mm, "mid": v(77.07, -87.07) * mm, "end": v(80, -80) * mm});
            skLineSegment(sketch, "E79.6", {"start": v(80, -80) * mm, "end": v(80, 80) * mm});
            skArc(sketch, "E79.7", {"start": v(80, 80) * mm, "mid": v(77.07, 87.07) * mm, "end": v(70, 90) * mm});
            skLineSegment(sketch, "E79.8", {"start": v(60, 40.3) * mm, "end": v(60, -40.3) * mm});
            skArc(sketch, "E79.9", {"start": v(-56.15, -48.18) * mm, "mid": v(0, -67.5) * mm, "end": v(56.15, -48.18) * mm});
            skArc(sketch, "E79.10", {"start": v(56.15, -48.18) * mm, "mid": v(58.99, -44.68) * mm, "end": v(60, -40.3) * mm});
            skArc(sketch, "E79.11", {"start": v(60, 40.3) * mm, "mid": v(58.99, 44.68) * mm, "end": v(56.15, 48.18) * mm});
            skArc(sketch, "E79.12", {"start": v(56.15, 48.18) * mm, "mid": v(0, 67.5) * mm, "end": v(-56.15, 48.18) * mm});
            skArc(sketch, "E79.13", {"start": v(-56.15, 48.18) * mm, "mid": v(-58.99, 44.68) * mm, "end": v(-60, 40.3) * mm});
            skLineSegment(sketch, "E79.14", {"start": v(-60, 40.3) * mm, "end": v(-60, -40.3) * mm});
            skArc(sketch, "E79.15", {"start": v(-60, -40.3) * mm, "mid": v(-58.99, -44.68) * mm, "end": v(-56.15, -48.18) * mm});
            skCircle(sketch, "E79.16", {"center": v(-60, -67.5) * mm, "radius": 4 * mm});
            skCircle(sketch, "E79.17", {"center": v(60, -67.5) * mm, "radius": 4 * mm});
            skCircle(sketch, "E79.18", {"center": v(60, 67.5) * mm, "radius": 4 * mm});
            skCircle(sketch, "E79.19", {"center": v(-60, 67.5) * mm, "radius": 4 * mm});
            skLineSegment(sketch, "E80", {"start": v(-32.72, 90) * mm, "end": v(-14.72, 108) * mm});
            skLineSegment(sketch, "E81", {"start": v(-14.72, 108) * mm, "end": v(-14.72, 120) * mm});
            skLineSegment(sketch, "E82", {"start": v(31.46, 90) * mm, "end": v(15.19, 106.28) * mm});
            skLineSegment(sketch, "E83", {"start": v(15.19, 106.28) * mm, "end": v(15.19, 118.28) * mm});
            skLineSegment(sketch, "E84", {"start": v(0, 90) * mm, "end": v(0, 120) * mm, "construction": true});
            skCircle(sketch, "E85", {"center": v(0, 120) * mm, "radius": 6 * mm});
            skArc(sketch, "E86", {"start": v(15.19, 118.28) * mm, "mid": v(1.15, 134.98) * mm, "end": v(-14.72, 120) * mm});
            skLineSegment(sketch, "E87", {"start": v(-80, 0) * mm, "end": v(80, 0) * mm, "construction": true});
            skLineSegment(sketch, "E88.MirrorCS", {"start": v(31.46, -90) * mm, "end": v(15.19, -106.28) * mm});
            skLineSegment(sketch, "E89.MirrorCS", {"start": v(15.19, -106.28) * mm, "end": v(15.19, -118.28) * mm});
            skArc(sketch, "E90.MirrorCS", {"start": v(15.19, -118.28) * mm, "mid": v(1.15, -134.98) * mm, "end": v(-14.72, -120) * mm});
            skLineSegment(sketch, "E91.MirrorCS", {"start": v(-14.72, -108) * mm, "end": v(-14.72, -120) * mm});
            skLineSegment(sketch, "E92.MirrorCS", {"start": v(-32.72, -90) * mm, "end": v(-14.72, -108) * mm});
            skCircle(sketch, "E93.MirrorC", {"center": v(0, -120) * mm, "radius": 6 * mm});
            skLineSegment(sketch, "E94.MirrorCS", {"start": v(0, -90) * mm, "end": v(0, -120) * mm, "construction": true});
            skSolve(sketch);
        }
        {
            var Q0;
            {var subQ0=sQuery(id+"F16.wireOp",EDGE,"E88.MirrorCS");Q0=makeQuery(id+"F16.imprint","IMPRINT",FACE,{"disambiguationData":[TD([[makeQuery(id+"F16.imprint","IMPRINT",EDGE,{"derivedFrom":subQ0}),-1.0]])]});}
            var Q1;
            {var subQ1=sQuery(id+"F16.wireOp",EDGE,"E80");Q1=makeQuery(id+"F16.imprint","IMPRINT",FACE,{"disambiguationData":[TD([[makeQuery(id+"F16.imprint","IMPRINT",EDGE,{"derivedFrom":subQ1}),-1.0]])]});}
            var Q2;
            {var subQ1=sQuery(id+"F16.wireOp",EDGE,"E79.1");Q2=makeQuery(id+"F16.imprint","IMPRINT",FACE,{"disambiguationData":[TD([[makeQuery(id+"F16.imprint","IMPRINT",EDGE,{"derivedFrom":subQ1}),1.0]])]});}
            var Q3;
            Q3=makeQuery(id+"F2.opExtrude","CAP_FACE",FACE,{"disambiguationData":[OSD([sQuery(id+"F0.wireOp",EDGE,"E12"),sQuery(id+"F0.wireOp",EDGE,"E13"),sQuery(id+"F0.wireOp",EDGE,"E14"),sQuery(id+"F0.wireOp",EDGE,"E15"),sQuery(id+"F0.wireOp",EDGE,"E17.filletArc"),sQuery(id+"F0.wireOp",EDGE,"E18.filletArc"),sQuery(id+"F0.wireOp",EDGE,"E19.filletArc"),sQuery(id+"F0.wireOp",EDGE,"E20.filletArc"),sQuery(id+"F0.wireOp",EDGE,"E25.0"),sQuery(id+"F0.wireOp",EDGE,"E25.1"),sQuery(id+"F0.wireOp",EDGE,"E25.2"),sQuery(id+"F0.wireOp",EDGE,"E25.3"),sQuery(id+"F0.wireOp",EDGE,"E25.4"),sQuery(id+"F0.wireOp",EDGE,"E25.5"),sQuery(id+"F0.wireOp",EDGE,"E25.6"),sQuery(id+"F0.wireOp",EDGE,"E25.7")])],"isStart":false});
            extrude(context, id + "F17", {"entities" : qUnion([Q0, Q1, Q2]), "endBound" : BoundingType.UP_TO_SURFACE, "endBoundEntityFace" : qUnion([Q3]), "depth" : 20 * mm});
        }
    });
